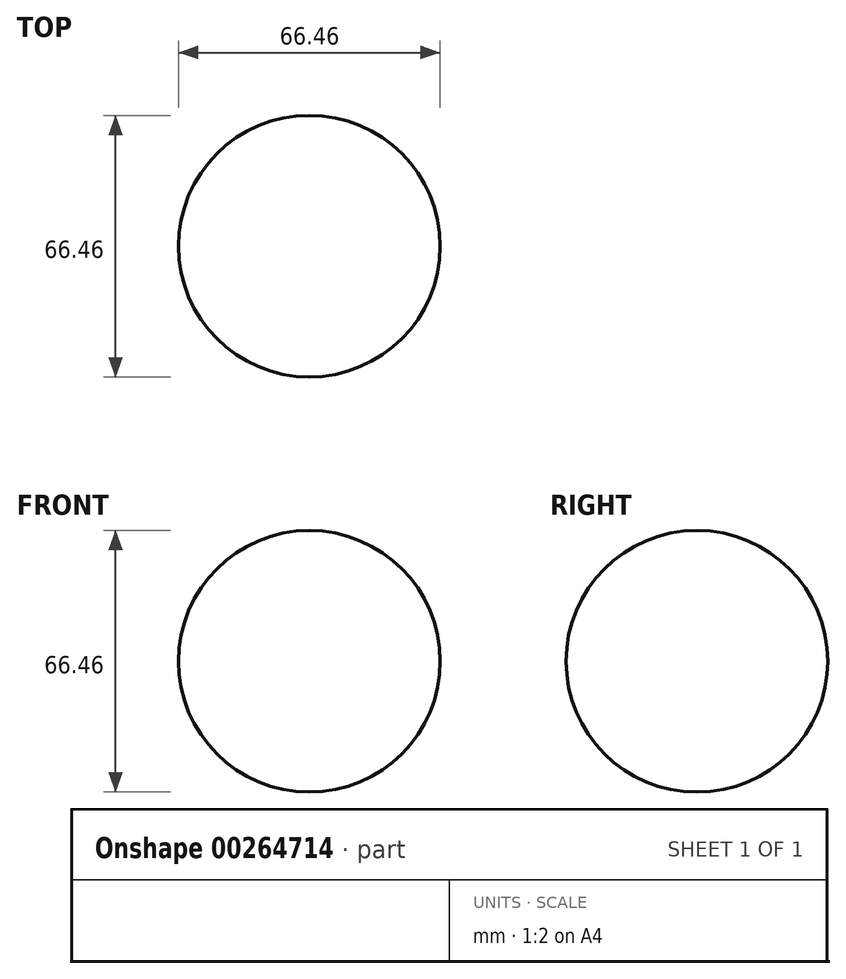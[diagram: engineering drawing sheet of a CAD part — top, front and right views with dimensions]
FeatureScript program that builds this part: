
annotation { "Feature Type Name" : "Feature", "Feature Type Description" : "" }
export const myFeature = defineFeature(function(context is Context, id is Id, definition is map)
    precondition{}
    {
        {
            var Q0;
            Q0=qCreatedBy(makeId("Front.planeOp"),FACE);
            var sketch = newSketch(context, id + "F0", { "sketchPlane" : qUnion([Q0])});
            skArc(sketch, "E0", {"start": v(0, 33.23) * mm, "mid": v(-33.23, 0) * mm, "end": v(0, -33.23) * mm});
            skLineSegment(sketch, "E1", {"start": v(0, 33.23) * mm, "end": v(0, -33.23) * mm});
            skSolve(sketch);
        }
        {
            var Q0;
            Q0=makeQuery(id+"F0.imprint","IMPRINT",FACE,{"disambiguationData":[TD([[makeQuery(id+"F0.imprint","IMPRINT",EDGE,{"derivedFrom":sQuery(id+"F0.wireOp",EDGE,"E0")}),1.0]])]});
            var Q1;
            Q1=sQuery(id+"F0.wireOp",EDGE,"E1");
            revolve(context, id + "F1", {"entities" : qUnion([Q0]), "axis" : qUnion([Q1]), "revolveType" : RevolveType.FULL});
        }
    });
